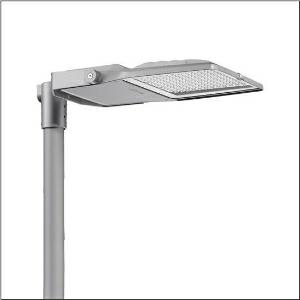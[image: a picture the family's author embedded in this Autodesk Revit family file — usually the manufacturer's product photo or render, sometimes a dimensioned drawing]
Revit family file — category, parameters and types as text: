
# Revit family: floodlight_fl_21_iq_midi___pl64_5xa7781e2e3a_93f0
name_source: partatom
category: Lighting Fixtures
units: mm (PartAtom-declared; Revit-internal decimal feet)

## family parameters
Cut with Voids When Loaded = No
Host = Face
Light Source = No
Part Type = Normal
Room Calculation Point = No
Round Connector Dimension = Use Diameter
Shared = No

## types (1)
- --- (1 x LED, 25930 lm, 208.1 W, 3000K)
    Apparent Load = 208 VA
    CIE Flux Codes = 28 80 98 100 100
    Color Rendering = 70
    Color Temperature = 3000K
    Default Elevation = 1800 mm
    Description = Floodlight FL 21 iQ midi, floodlight, primary light control with lens, of PMMA, primary optical cover: protective disc, of toughened safety glass, transparent, light distribution: PL64, light emission: direct distribution, installation type: surface-mounted, LED, High Power LED, rated luminous flux: 25.930lm, luminous efficacy: 125lm/W, light colour: 730, colour temperature: 3000K, control gear: iQ Comfort/DALI, control: optimised constant luminous flux control (CLO 2.0), Desk-Remote (wireless, voltage-free reading and setting of iQ features in the workshop via application-optimized NFC function/RFID function), Light-Fading, Smart-Wire, Night-Set, Lumen-Switch, Temp-Guard, Auto-Match, with terminal, 6-pole, mains connection: 220..240V, AC, 50/60Hz, start of lifetime: 208W, end of service life: 227W, reduction: 90W, luminaire housing, of diecast aluminium, powder-coated, Siteco® metallic grey (DB 702S), corrosivity category C5 mid according to DIN EN ISO 12944, suitable for swimming pools, chlorine-resistant, sealing non-destructively replaceable, please order mast flange separately, mast bracket, of steel, galvanised, powder-coated, Siteco® metallic grey (DB 702S), protection rating (complete): IP66, insulation class (complete): insulation class II (safety insulation), certification: CE, ENEC, VDE, protection symbol: D, impact resistance: IK08, permissible operating ambient temperature: -40..+40°C, permissible operating ambient temperature for outdoor applications: -40..+50°C, standard: DIN EN 12944, LABS conformity tested according to VDMA 24364:2018-05, packaging unit: 1 piece

Light Distribution: PL64
    Height = 76 mm
    Lamp = 1 x LED
    Lamp Light Flux = 25930 lm
    Lamp Power = 208.1 W
    Lamp count = 1
    Length = 657 mm
    Luminous efficacy = 125 lm/W
    Manufacturer = Siteco
    ModVariant = No
    Model = 5XA7781E2E3A
    Number of Poles = 1
    OnlyDefault = Yes
    Power Factor = 1
    Product Name = Floodlight FL 21 iQ midi | PL64
    Product group = floodlight | pylon annexe
    ProductGroupID = 6200
    Protection Class = Protection class II
    Protection Degree = IP 66
    RLX_Detail_Level = 1
    RLX_Emergency_Light_Flux = 0 lm
    RLX_Emergency_Type = 0
    RLX_Emergency_Type_DB = No
    RlxData = <blob elided: 153881 chars, md5=70a356ba>
    Socket = socket
    Standby Power = 0 W
    System Light Flux = 25930 lm
    System Power = 208 W
    Type Comments = factory setting: luminous flux: 100 % | dim-lin: 254 | 710 mA
    Type Image = l_1007123.jpg
    URL = http://relux.com
    VarID = @adj_107286
    Voltage = 0 V
    Weight = 0.00 kg
    Width = 442 mm

## geometry (parser evidence)
native form markers: Blend x4, Sweep x11
no freeform markers — native parametric forms only
